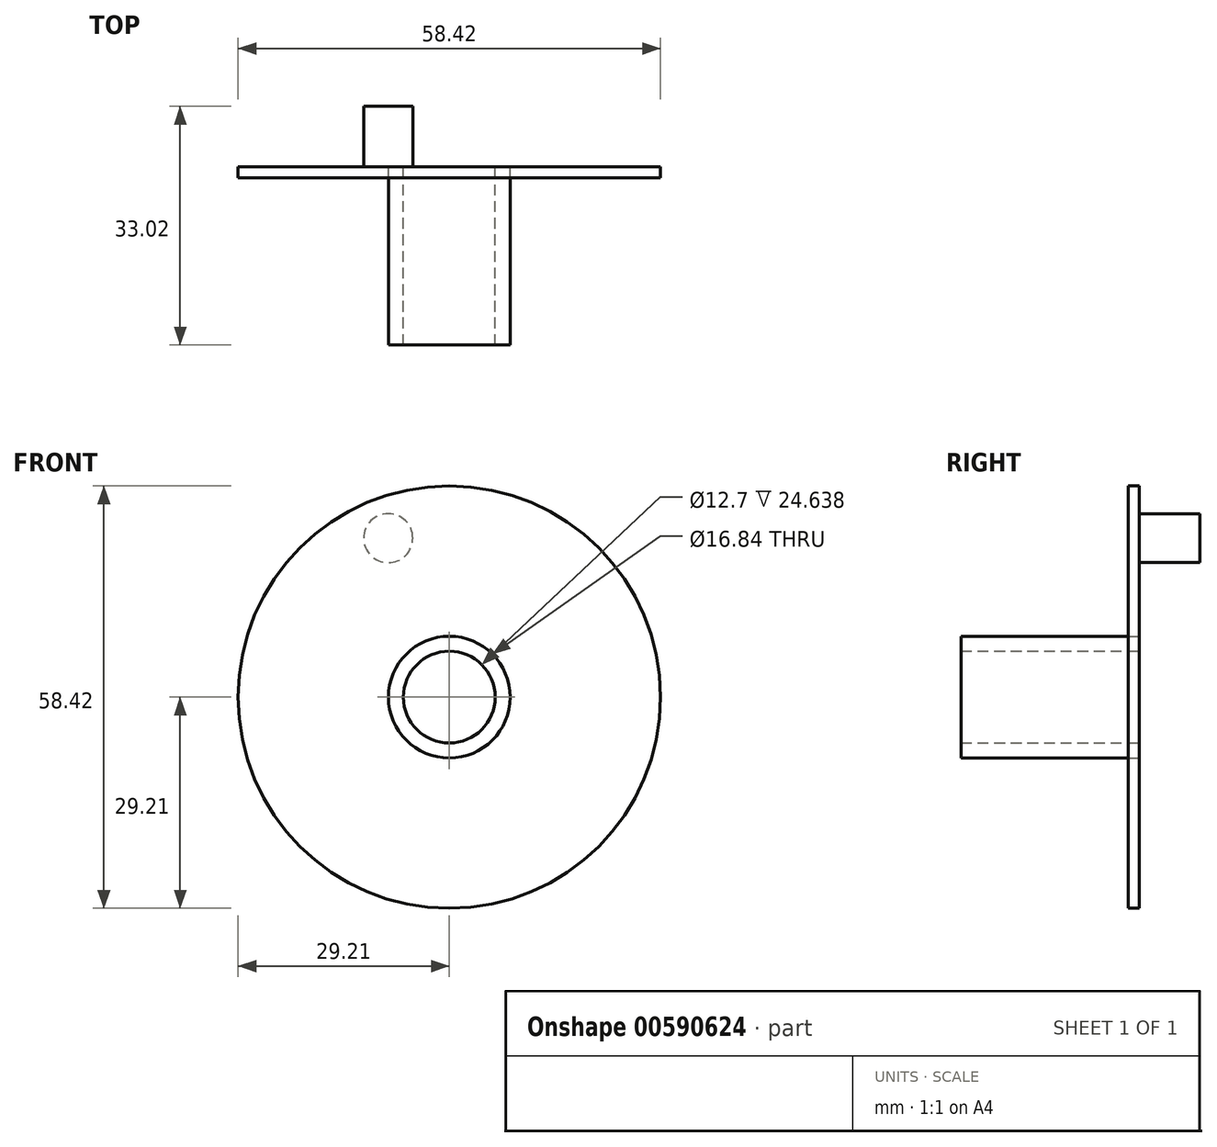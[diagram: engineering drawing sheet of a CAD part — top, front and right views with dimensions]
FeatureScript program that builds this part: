
annotation { "Feature Type Name" : "Feature", "Feature Type Description" : "" }
export const myFeature = defineFeature(function(context is Context, id is Id, definition is map)
    precondition{}
    {
        {
            var Q0;
            Q0=qCreatedBy(makeId("Front.planeOp"),FACE);
            var sketch = newSketch(context, id + "F0", { "sketchPlane" : qUnion([Q0])});
            skCircle(sketch, "E0", {"center": v(0, 0) * mm, "radius": 6.35 * mm});
            skCircle(sketch, "E1", {"center": v(0, 0) * mm, "radius": 29.21 * mm});
            skCircle(sketch, "E2", {"center": v(0, 0) * mm, "radius": 8.42 * mm});
            skSolve(sketch);
        }
        {
            var Q0;
            Q0 = qSketchRegion(id + "F0", true);
            extrude(context, id + "F1", {"entities" : qUnion([Q0]), "depth" : 1.52 * mm, "offsetDistance" : 25.4 * mm});
        }
        {
            var Q0;
            Q0=makeQuery(id+"F0.imprint","IMPRINT",FACE,{"disambiguationData":[TD([[makeQuery(id+"F0.imprint","IMPRINT",EDGE,{"derivedFrom":sQuery(id+"F0.wireOp",EDGE,"E0")}),-1.0]])]});
            extrude(context, id + "F2", {"entities" : qUnion([Q0]), "depth" : 24.64 * mm, "offsetDistance" : 25.4 * mm});
        }
        {
            var Q0;
            Q0=makeQuery(id+"F1.opExtrude","CAP_FACE",FACE,{"disambiguationData":[OSD([sQuery(id+"F0.wireOp",EDGE,"E1"),sQuery(id+"F0.wireOp",EDGE,"E2")])],"isStart":true});
            var sketch = newSketch(context, id + "F3", { "sketchPlane" : qUnion([Q0])});
            skCircle(sketch, "E3", {"center": v(8.45, 22) * mm, "radius": 3.4 * mm});
            skSolve(sketch);
        }
        {
            var Q0;
            Q0 = qSketchRegion(id + "F3", true);
            extrude(context, id + "F4", {"entities" : qUnion([Q0]), "operationType" : NewBodyOperationType.ADD, "depth" : 8.38 * mm, "offsetDistance" : 25.4 * mm});
        }
    });
